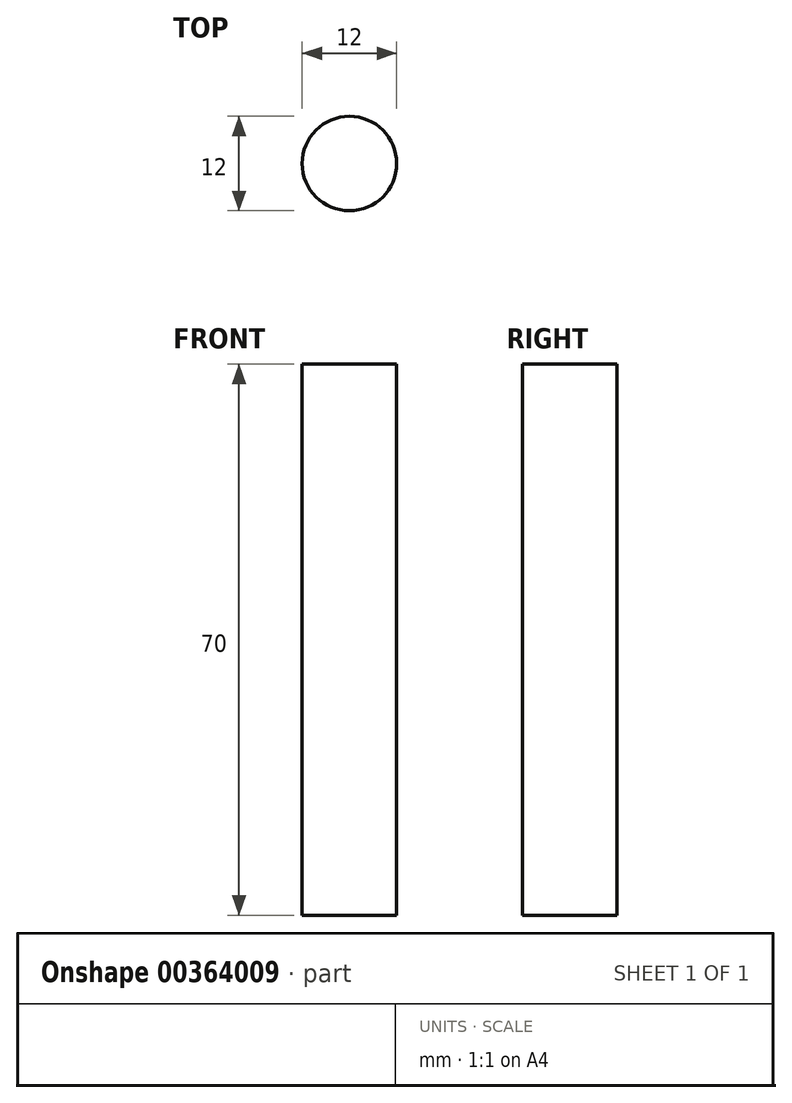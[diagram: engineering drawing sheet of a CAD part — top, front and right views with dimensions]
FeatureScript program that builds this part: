
annotation { "Feature Type Name" : "Feature", "Feature Type Description" : "" }
export const myFeature = defineFeature(function(context is Context, id is Id, definition is map)
    precondition{}
    {
        {
            var Q0;
            Q0=qCreatedBy(makeId("Top.planeOp"), FACE);
            var sketch = newSketch(context, id + "F0", { "sketchPlane" : qUnion([Q0])});
            skCircle(sketch, "E0", {"center": v(0, 0) * mm, "radius": 6 * mm});
            skSolve(sketch);
        }
        {
            var Q0;
            Q0 = qSketchRegion(id + "F0", true);
            extrude(context, id + "F1", {"entities" : qUnion([Q0]), "flatOperationType" : FlatOperationType.REMOVE, "depth" : 70 * mm, "offsetDistance" : 25 * mm, "domain" : OperationDomain.MODEL});
        }
    });
